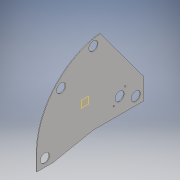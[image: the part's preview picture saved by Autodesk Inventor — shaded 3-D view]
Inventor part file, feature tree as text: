
AUTODESK INVENTOR PART (.ipt)
format: ipt  version: 2018 (Build 220112000, 112)  size: 187,392 bytes
history: native  units: in
note: dims shown in document units (in); Inventor stores cm internally (conversion verified against a paired STEP export)
features: extrude x5, sketch x4, plane x2, projected_geometry x1
ambient origin geometry x8: Origin, YZ Plane, XZ Plane, XY Plane, X Axis, Y Axis, Z Axis, Center Point
bodies: Body1 (feature_tree)
feature tree (12):
  sketch  "Sketch1"  dims[d2=1.1225in d5=11.0in]
  plane  "Work Plane2"
  sketch  "Sketch2"  dims[d8=1.0in d9=1.0in]
  plane  "Work Plane1"
  extrude  "Extrusion6"  Depth=11.0in
  extrude  "Extrusion7"  Depth=1.0in
  extrude  "Extrusion8"  Depth=8.0in
  extrude  "Extrusion9"  Depth=0.07in
  extrude  "Extrusion10"  Depth=0.07in
  sketch  "Sketch4"  dims[d11=6.0in d12=8.0in]
  projected_geometry  "Projected Loop1"
  sketch  "Sketch5"  dims[d13=1.125in d14=5.5in d15=2.0in d16=1.125in d22=10.0in d24=1.0in d25=1.125in d28=2.0in d29=1.0in d30=2.0in d31=1.125in d34=9.0in d35=1.5in d36=12.25in d37=0.707in d38=0.707in d39=0.707in d40=0.707in d45=0.159in d46=0.159in d47=1.0in d48=2.0in d49=1.0in d50=1.125in d51=0.07in d52=0.0in d53=0.07in d54=0.0in d55=0.07in d56=0.0in d57=0.07in d58=0.0in d59=0.07in d60=0.0in]
